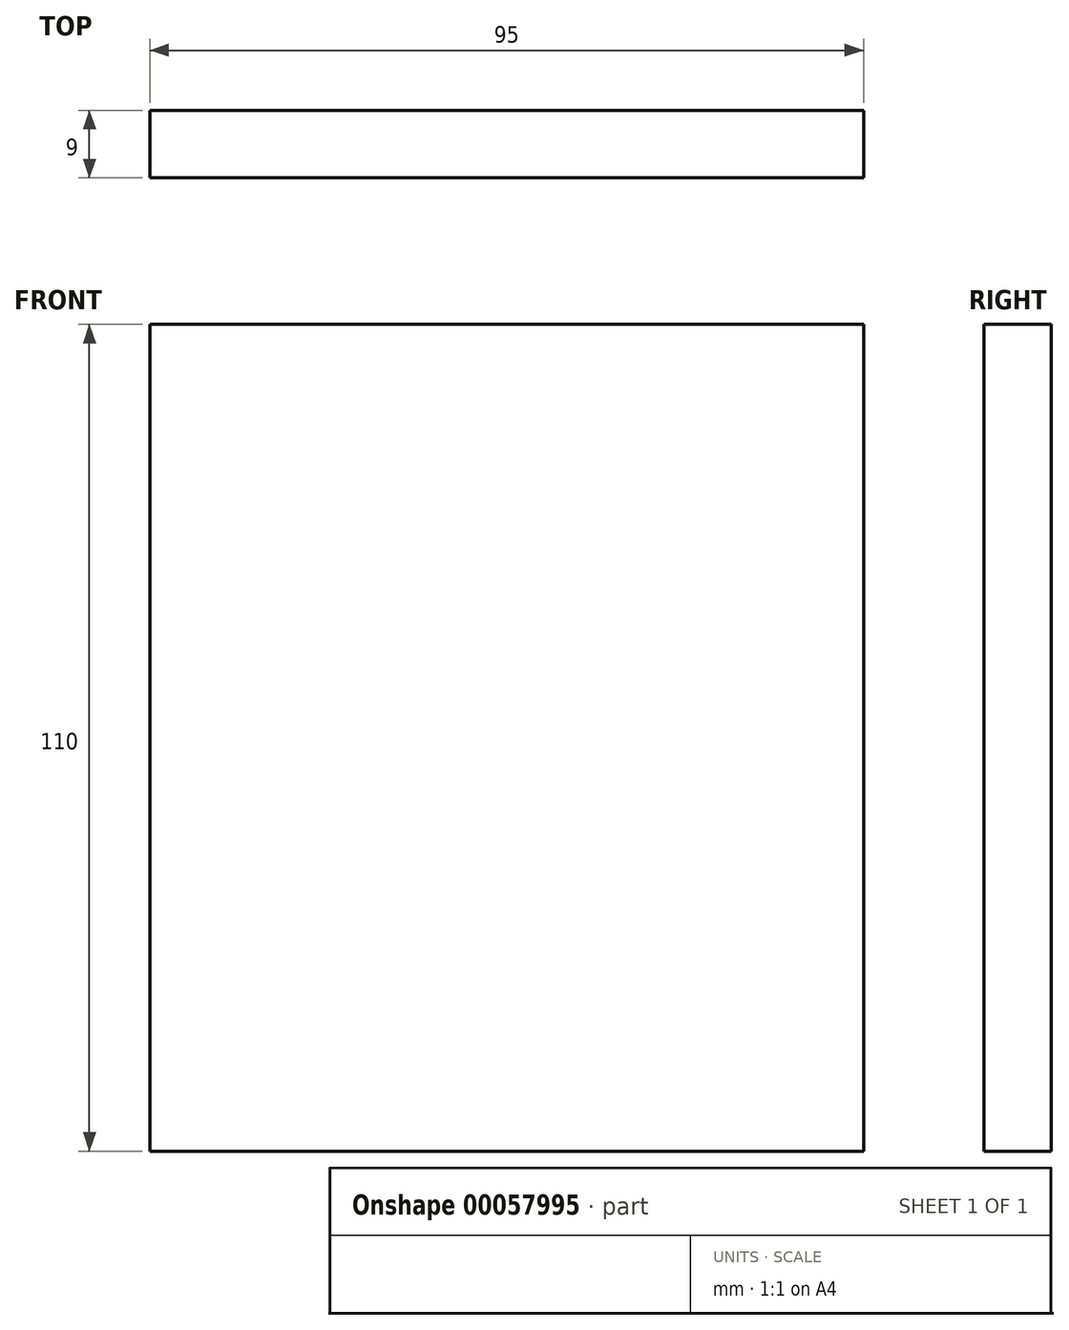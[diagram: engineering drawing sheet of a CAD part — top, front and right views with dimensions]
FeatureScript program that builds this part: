
annotation { "Feature Type Name" : "Feature", "Feature Type Description" : "" }
export const myFeature = defineFeature(function(context is Context, id is Id, definition is map)
    precondition{}
    {
        {
            var Q0;
            Q0=qCreatedBy(makeId("Front.planeOp"),FACE);
            var sketch = newSketch(context, id + "F0", { "sketchPlane" : qUnion([Q0])});
            skLineSegment(sketch, "E0.rect.bottom", {"start": v(47.5, -55) * mm, "end": v(-47.5, -55) * mm});
            skLineSegment(sketch, "E0.rect.top", {"start": v(47.5, 55) * mm, "end": v(-47.5, 55) * mm});
            skLineSegment(sketch, "E0.rect.left", {"start": v(47.5, -55) * mm, "end": v(47.5, 55) * mm});
            skLineSegment(sketch, "E0.rect.right", {"start": v(-47.5, -55) * mm, "end": v(-47.5, 55) * mm});
            skPoint(sketch, "E0.rect.middle", {"position": v(0, 0) * mm});
            skSolve(sketch);
        }
        {
            var Q0;
            Q0 = qSketchRegion(id + "F0", true);
            extrude(context, id + "F1", {"entities" : qUnion([Q0]), "depth" : 9 * mm});
        }
    });
